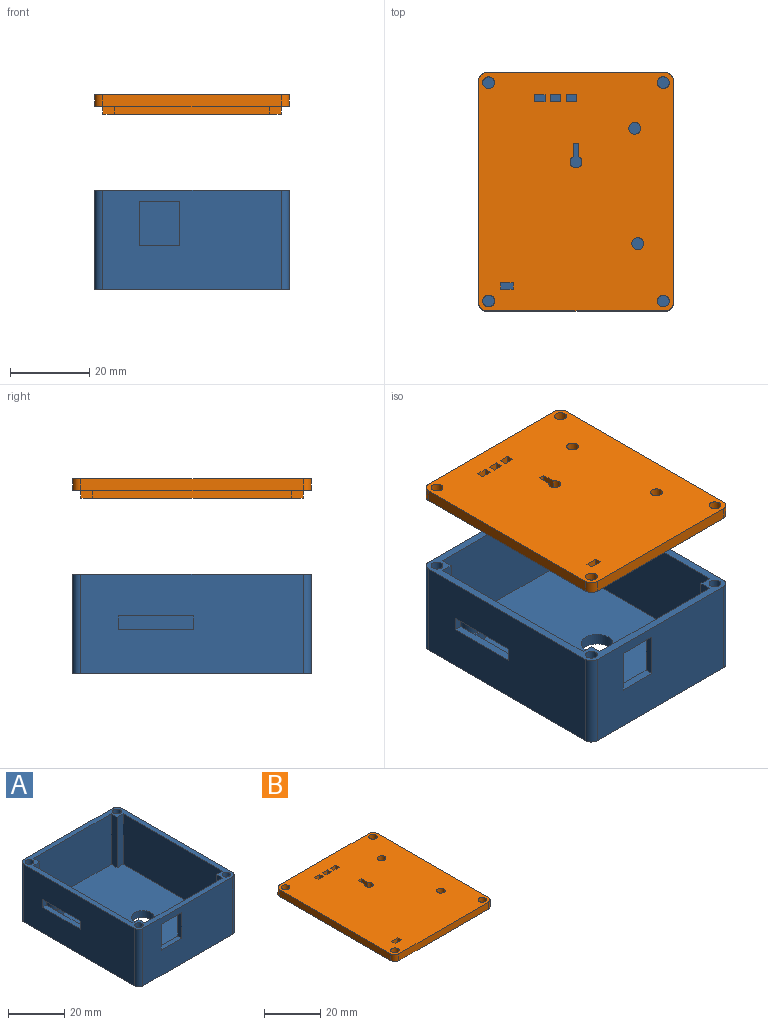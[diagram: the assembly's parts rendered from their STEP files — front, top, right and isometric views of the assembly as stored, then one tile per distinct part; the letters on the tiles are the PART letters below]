
ASSEMBLY  parts=2 mates=1
PART A: 64 faces, bbox 49x60x25 mm
  f0: plane 60x49mm, normal (0,0,-1), area 2839.5mm2, adj f1,f3,f8,f9,f45,f46,f47,f48
  f1: plane 56x25mm, normal (-1,0,0), area 1333.5mm2, adj f0,f7,f37,f38,f39,f40,f60,f63
  f2: plane 50x22mm, normal (1,0,0), area 1033.5mm2, adj f5,f6,f7,f12,f37,f38,f39,f40
  f3: plane 45x25mm, normal (0,-1,0), area 1010.2mm2, adj f0,f7,f33,f34,f35,f36,f60,f61
  f4: plane 39x22mm, normal (0,1,0), area 743.2mm2, adj f7,f12,f22,f23,f33,f34,f35,f36
  f5: plane 22x3mm, normal (0,-1,0), area 66mm2, adj f2,f7,f12,f25
  f6: plane 22x3mm, normal (0,1,0), area 66mm2, adj f2,f7,f12,f23
  f7: plane 60x49mm, normal (0,0,1), area 424.3mm2, adj f1,f2,f3,f4,f5,f6,f8,f9
  f8: plane 56x25mm, normal (1,0,0), area 1400mm2, adj f0,f7,f61,f62
  f9: plane 45x25mm, normal (0,1,0), area 1125mm2, adj f0,f7,f62,f63
  f10: plane 22x3mm, normal (0,1,0), area 66mm2, adj f7,f12,f21,f22
  f11: plane 22x3mm, normal (0,-1,0), area 66mm2, adj f7,f12,f21,f26
  f12: plane 56x45mm, normal (0,0,1), area 2356.8mm2, adj f2,f4,f5,f6,f10,f11,f21,f22
  f13: cylinder r=1.5mm len=8mm, axis (0,0,1), area 75.4mm2, adj f7,f14
  f14: plane 3x3mm, normal (0,0,1), area 7.1mm2, adj f13
  f15: cylinder r=1.5mm len=8mm, axis (0,0,1), area 75.4mm2, adj f7,f16
  f16: plane 3x3mm, normal (0,0,1), area 7.1mm2, adj f15
  f17: cylinder r=1.5mm len=8mm, axis (0,0,1), area 75.4mm2, adj f7,f18
  f18: plane 3x3mm, normal (0,0,1), area 7.1mm2, adj f17
  f19: cylinder r=1.5mm len=8mm, axis (0,0,1), area 75.4mm2, adj f7,f20
  f20: plane 3x3mm, normal (0,0,1), area 7.1mm2, adj f19
  f21: plane 50x22mm, normal (-1,0,0), area 1100mm2, adj f7,f10,f11,f12
  f22: plane 22x3mm, normal (-1,0,0), area 66mm2, adj f4,f7,f10,f12
  f23: plane 22x3mm, normal (1,0,0), area 66mm2, adj f4,f6,f7,f12
  f24: plane 39x22mm, normal (0,-1,0), area 858mm2, adj f7,f12,f25,f26
  f25: plane 22x3mm, normal (1,0,0), area 66mm2, adj f5,f7,f12,f24
  f26: plane 22x3mm, normal (-1,0,0), area 66mm2, adj f7,f11,f12,f24
  f27: cylinder r=1.5mm len=9mm, axis (0,0,-1), area 84.8mm2, adj f29,f58
  f28: cylinder r=3mm len=6mm, axis (0,0,-1), area 94.2mm2, adj f29,f42
  f29: plane 6x6mm, normal (0,0,1), area 21.2mm2, adj f27,f28
  f30: cylinder r=1.5mm len=9mm, axis (0,0,-1), area 84.8mm2, adj f32,f51
  f31: cylinder r=3mm len=6mm, axis (0,0,-1), area 94.2mm2, adj f32,f44
  f32: plane 6x6mm, normal (0,0,1), area 21.2mm2, adj f30,f31
  f33: plane 10.2x2mm, normal (0,0,-1), area 20.4mm2, adj f3,f4,f34,f36
  f34: plane 11.25x2mm, normal (1,0,0), area 22.5mm2, adj f3,f4,f33,f35
  f35: plane 10.2x2mm, normal (0,0,1), area 20.4mm2, adj f3,f4,f34,f36
  f36: plane 11.25x2mm, normal (-1,0,0), area 22.5mm2, adj f3,f4,f33,f35
  f37: plane 19x2mm, normal (0,0,-1), area 38mm2, adj f1,f2,f38,f40
  f38: plane 3.5x2mm, normal (0,-1,0), area 7mm2, adj f1,f2,f37,f39
  f39: plane 19x2mm, normal (0,0,1), area 38mm2, adj f1,f2,f38,f40
  f40: plane 3.5x2mm, normal (0,1,0), area 7mm2, adj f1,f2,f37,f39
  f41: cylinder r=3.5mm len=7mm, axis (0,0,-1), area 66mm2, adj f12,f42
  f42: plane 7x7mm, normal (0,0,1), area 10.2mm2, adj f28,f41
  f43: cylinder r=3.5mm len=7mm, axis (0,0,-1), area 66mm2, adj f12,f44
  f44: plane 7x7mm, normal (0,0,1), area 10.2mm2, adj f31,f43
  f45: plane 2.52x2mm, normal (0.84,0.54,0), area 6mm2, adj f0,f46,f50,f51
  f46: plane 2.67x2mm, normal (0.89,-0.46,0), area 6mm2, adj f0,f45,f47,f51
  f47: plane 3x2mm, normal (0.05,-1,0), area 6mm2, adj f0,f46,f48,f51
  f48: plane 2.52x2mm, normal (-0.84,-0.54,0), area 6mm2, adj f0,f47,f49,f51
  f49: plane 2.67x2mm, normal (-0.89,0.46,0), area 6mm2, adj f0,f48,f50,f51
  f50: plane 3x2mm, normal (-0.05,1,0), area 6mm2, adj f0,f45,f49,f51
  f51: plane 5.99x5.34mm, normal (0,0,-1), area 16.3mm2, adj f30,f45,f46,f47,f48,f49,f50
  f52: plane 2.49x2mm, normal (0.83,0.56,0), area 6mm2, adj f0,f53,f57,f58
  f53: plane 2.7x2mm, normal (0.9,-0.44,0), area 6mm2, adj f0,f52,f54,f58
  f54: plane 2.99x2mm, normal (0.07,-1,0), area 6mm2, adj f0,f53,f55,f58
  f55: plane 2.49x2mm, normal (-0.83,-0.56,0), area 6mm2, adj f0,f54,f56,f58
  f56: plane 2.7x2mm, normal (-0.9,0.44,0), area 6mm2, adj f0,f55,f57,f58
  f57: plane 2.99x2mm, normal (-0.07,1,0), area 6mm2, adj f0,f52,f56,f58
  f58: plane 5.99x5.39mm, normal (0,0,-1), area 16.3mm2, adj f27,f52,f53,f54,f55,f56,f57
  f59: cylinder r=4mm len=8mm, axis (0,0,1), area 75.4mm2, adj f0,f12
  f60: cylinder r=2mm len=25mm, axis (0,0,-1), area 78.5mm2, adj f0,f1,f3,f7
  f61: cylinder r=2mm len=25mm, axis (0,0,1), area 78.5mm2, adj f0,f3,f7,f8
  f62: cylinder r=2mm len=25mm, axis (0,0,-1), area 78.5mm2, adj f0,f7,f8,f9
  f63: cylinder r=2mm len=25mm, axis (0,0,1), area 78.5mm2, adj f0,f1,f7,f9
PART B: 49 faces, bbox 49x60x5 mm
  f0: plane 3x2mm, normal (0,1,0), area 6mm2, adj f1,f40,f42,f46
  f1: plane 60x49mm, normal (0,0,-1), area 424.3mm2, adj f0,f2,f3,f4,f5,f6,f8,f9
  f2: plane 3x2mm, normal (0,-1,0), area 6mm2, adj f1,f40,f42,f45
  f3: plane 56x3mm, normal (-1,0,0), area 168mm2, adj f1,f7,f34,f37
  f4: plane 45x3mm, normal (0,-1,0), area 135mm2, adj f1,f7,f34,f35
  f5: plane 56x3mm, normal (1,0,0), area 168mm2, adj f1,f7,f35,f36
  f6: plane 45x3mm, normal (0,1,0), area 135mm2, adj f1,f7,f36,f37
  f7: plane 60x49mm, normal (0,0,1), area 2862.4mm2, adj f3,f4,f5,f6,f8,f9,f10,f11
  f8: cylinder r=1.5mm len=3mm, axis (0,0,1), area 28.3mm2, adj f1,f7
  f9: cylinder r=1.5mm len=3mm, axis (0,0,1), area 28.3mm2, adj f1,f7
  f10: cylinder r=1.5mm len=3mm, axis (0,0,1), area 28.3mm2, adj f1,f7
  f11: cylinder r=1.5mm len=3mm, axis (0,0,1), area 28.3mm2, adj f1,f7
  f12: plane 5x1.8mm, normal (1,0,0), area 9mm2, adj f7,f13,f15,f40
  f13: plane 5x2.7mm, normal (0,1,0), area 13.5mm2, adj f7,f12,f14,f40
  f14: plane 5x1.8mm, normal (-1,0,0), area 9mm2, adj f7,f13,f15,f40
  f15: plane 5x2.7mm, normal (0,-1,0), area 13.5mm2, adj f7,f12,f14,f40
  f16: plane 5x1.8mm, normal (1,0,0), area 9mm2, adj f7,f17,f19,f40
  f17: plane 5x2.7mm, normal (0,1,0), area 13.5mm2, adj f7,f16,f18,f40
  f18: plane 5x1.8mm, normal (-1,0,0), area 9mm2, adj f7,f17,f19,f40
  f19: plane 5x2.7mm, normal (0,-1,0), area 13.5mm2, adj f7,f16,f18,f40
  f20: plane 5x1.8mm, normal (1,0,0), area 9mm2, adj f7,f21,f23,f40
  f21: plane 5x2.7mm, normal (0,1,0), area 13.5mm2, adj f7,f20,f22,f40
  f22: plane 5x1.8mm, normal (-1,0,0), area 9mm2, adj f7,f21,f23,f40
  f23: plane 5x2.7mm, normal (0,-1,0), area 13.5mm2, adj f7,f20,f22,f40
  f24: cylinder r=1.5mm len=5mm, axis (0,0,1), area 47.1mm2, adj f7,f40
  f25: cylinder r=1.5mm len=5mm, axis (0,0,1), area 47.1mm2, adj f7,f40
  f26: plane 5x1.69mm, normal (1,0,0), area 8.5mm2, adj f7,f27,f29,f40
  f27: plane 5x3.11mm, normal (0,1,0), area 15.6mm2, adj f7,f26,f28,f40
  f28: plane 5x1.69mm, normal (-1,0,0), area 8.5mm2, adj f7,f27,f29,f40
  f29: plane 5x3.11mm, normal (0,-1,0), area 15.6mm2, adj f7,f26,f28,f40
  f30: plane 5x3.36mm, normal (1,0,0), area 16.8mm2, adj f7,f31,f33,f40
  f31: cylinder r=1.5mm len=5mm, axis (0,0,1), area 39.3mm2, adj f7,f30,f32,f40
  f32: plane 5x3.36mm, normal (-1,0,0), area 16.8mm2, adj f7,f31,f33,f40
  f33: plane 5x1.5mm, normal (0,-1,0), area 7.5mm2, adj f7,f30,f32,f40
  f34: cylinder r=2mm len=3mm, axis (0,0,-1), area 9.4mm2, adj f1,f3,f4,f7
  f35: cylinder r=2mm len=3mm, axis (0,0,1), area 9.4mm2, adj f1,f4,f5,f7
  f36: cylinder r=2mm len=3mm, axis (0,0,-1), area 9.4mm2, adj f1,f5,f6,f7
  f37: cylinder r=2mm len=3mm, axis (0,0,1), area 9.4mm2, adj f1,f3,f6,f7
  f38: plane 3x2mm, normal (0,1,0), area 6mm2, adj f1,f40,f41,f48
  f39: plane 3x2mm, normal (0,-1,0), area 6mm2, adj f1,f40,f41,f43
  f40: plane 56x45mm, normal (0,0,-1), area 2438.1mm2, adj f0,f2,f12,f13,f14,f15,f16,f17
  f41: plane 50x2mm, normal (1,0,0), area 100mm2, adj f1,f38,f39,f40
  f42: plane 50x2mm, normal (-1,0,0), area 100mm2, adj f0,f1,f2,f40
  f43: plane 3x2mm, normal (1,0,0), area 6mm2, adj f1,f39,f40,f44
  f44: plane 39x2mm, normal (0,-1,0), area 78mm2, adj f1,f40,f43,f45
  f45: plane 3x2mm, normal (-1,0,0), area 6mm2, adj f1,f2,f40,f44
  f46: plane 3x2mm, normal (-1,0,0), area 6mm2, adj f0,f1,f40,f47
  f47: plane 39x2mm, normal (0,1,0), area 78mm2, adj f1,f40,f46,f48
  f48: plane 3x2mm, normal (1,0,0), area 6mm2, adj f1,f38,f40,f47
PLACE A at identity fixed
PLACE B t=(-73.81,1.8,46.1)mm
MATE slider A.f17 <-> B.f11  axis (0,0,1) through (-64.27,9.85,25)mm
